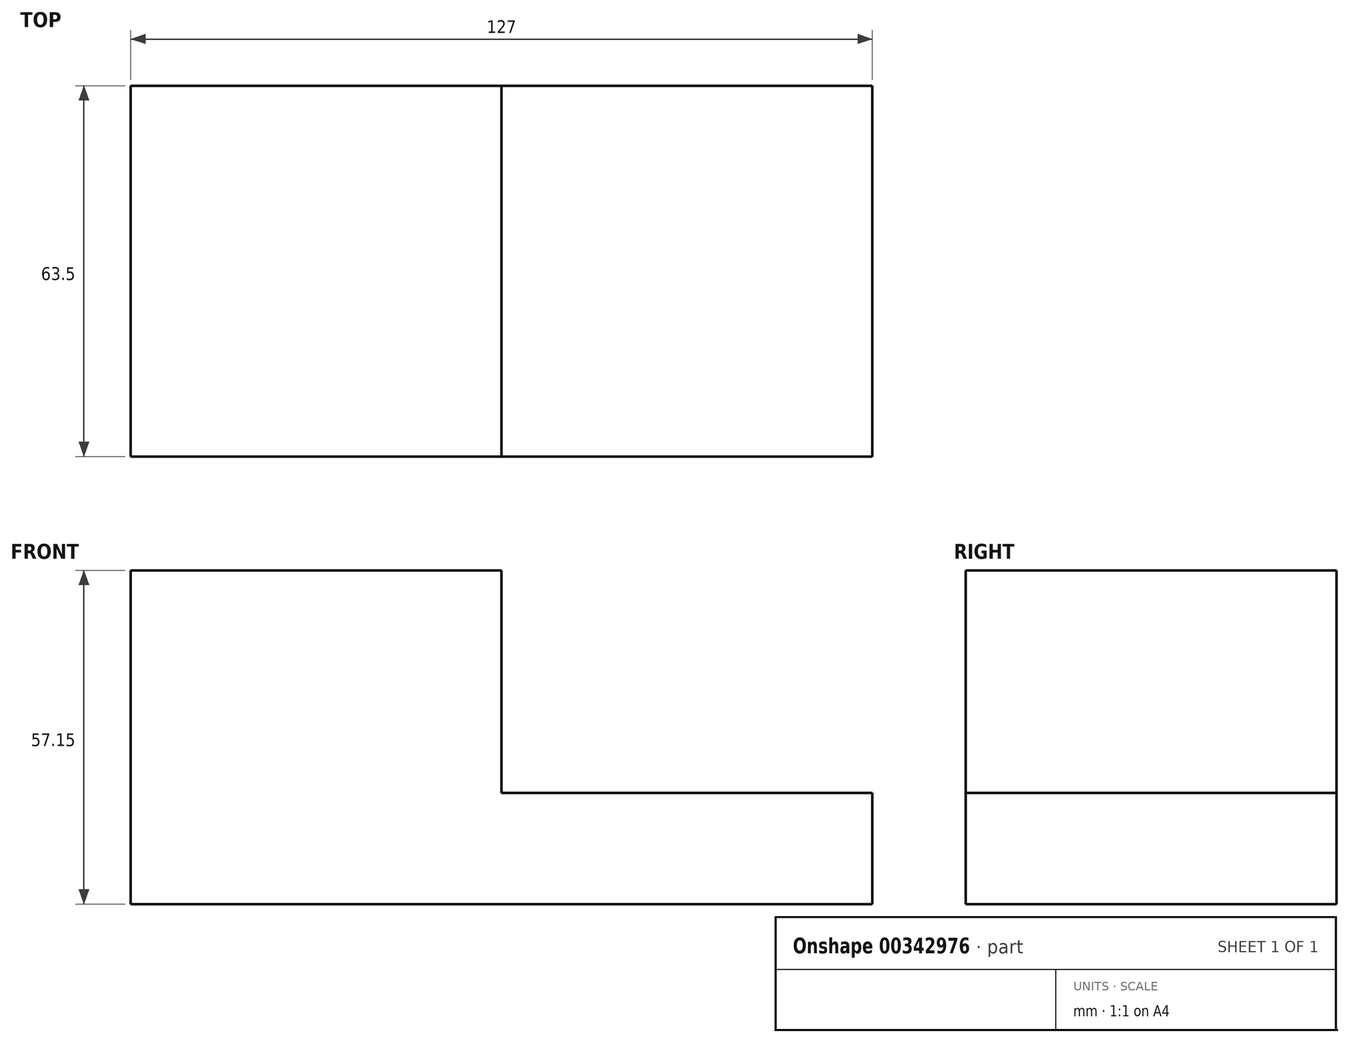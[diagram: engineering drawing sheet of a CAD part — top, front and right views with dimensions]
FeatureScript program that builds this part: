
annotation { "Feature Type Name" : "Feature", "Feature Type Description" : "" }
export const myFeature = defineFeature(function(context is Context, id is Id, definition is map)
    precondition{}
    {
        {
            var Q0;
            Q0=qCreatedBy(makeId("Front.planeOp"),FACE);
            var sketch = newSketch(context, id + "F0", { "sketchPlane" : qUnion([Q0])});
            skLineSegment(sketch, "E0", {"start": v(-63.5, -34.25) * mm, "end": v(63.5, -34.25) * mm});
            skLineSegment(sketch, "E1", {"start": v(63.5, -34.25) * mm, "end": v(63.5, -15.2) * mm});
            skLineSegment(sketch, "E2", {"start": v(63.5, -15.2) * mm, "end": v(0, -15.2) * mm});
            skLineSegment(sketch, "E3", {"start": v(0, -15.2) * mm, "end": v(0, 22.9) * mm});
            skLineSegment(sketch, "E4", {"start": v(0, 22.9) * mm, "end": v(-63.5, 22.9) * mm});
            skLineSegment(sketch, "E5", {"start": v(-63.5, 22.9) * mm, "end": v(-63.5, -34.25) * mm});
            skSolve(sketch);
        }
        {
            var Q0;
            Q0 = qSketchRegion(id + "F0", true);
            extrude(context, id + "F1", {"entities" : qUnion([Q0]), "depth" : 63.5 * mm});
        }
    });
